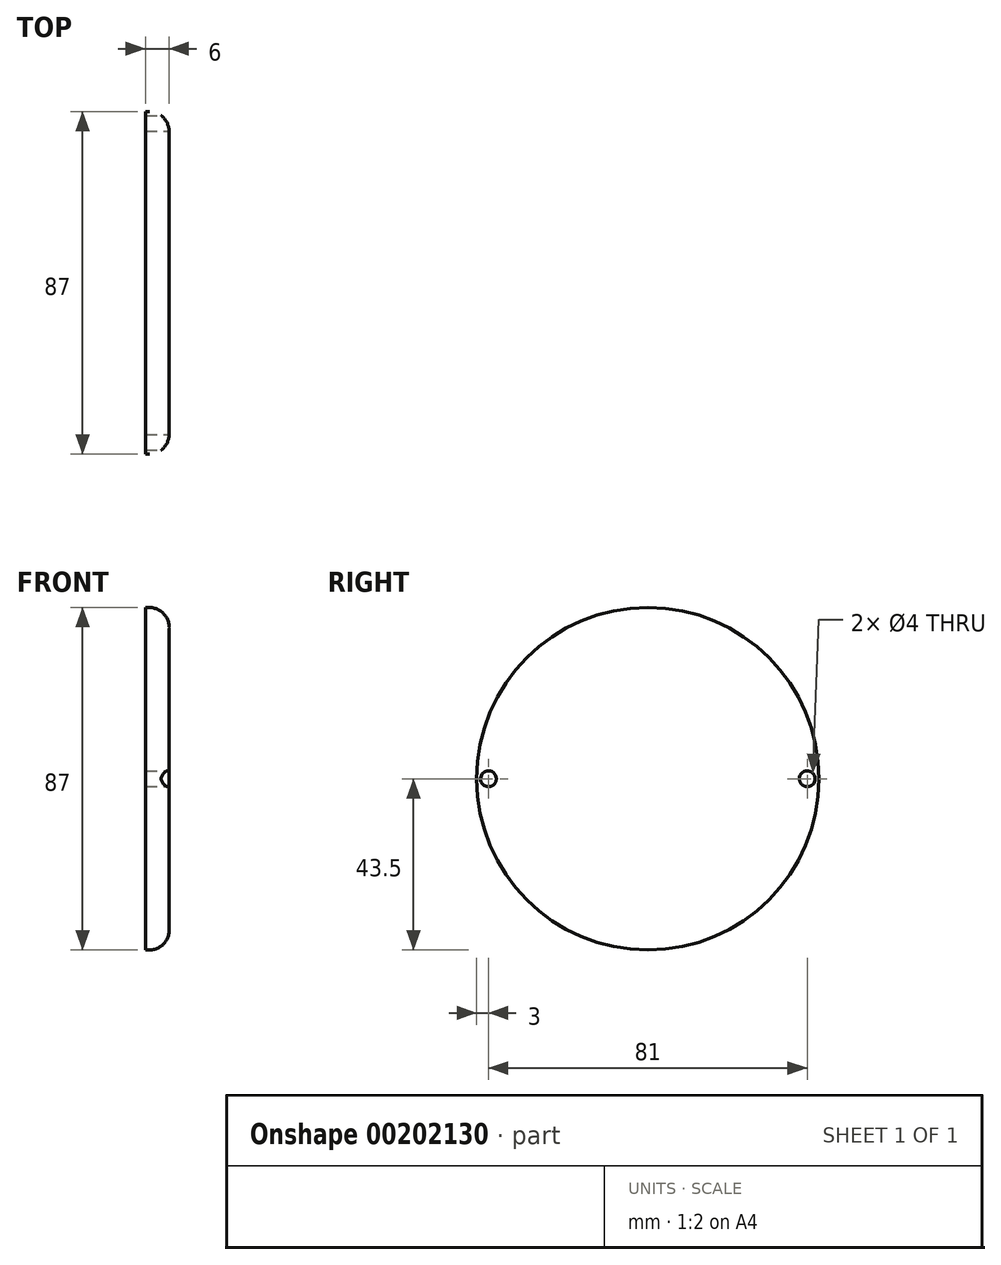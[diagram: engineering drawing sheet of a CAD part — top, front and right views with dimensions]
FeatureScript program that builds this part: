
annotation { "Feature Type Name" : "Feature", "Feature Type Description" : "" }
export const myFeature = defineFeature(function(context is Context, id is Id, definition is map)
    precondition{}
    {
        {
            var Q0;
            Q0=qCreatedBy(makeId("Right.planeOp"),FACE);
            var sketch = newSketch(context, id + "F0", { "sketchPlane" : qUnion([Q0])});
            skCircle(sketch, "E0", {"center": v(0, 0) * mm, "radius": 43.5 * mm});
            skCircle(sketch, "E1", {"center": v(-40.5, 0) * mm, "radius": 2 * mm});
            skCircle(sketch, "E2.MirrorC", {"center": v(40.5, 0) * mm, "radius": 2 * mm});
            skSolve(sketch);
        }
        {
            var Q0;
            Q0=makeQuery(id+"F0.imprint","IMPRINT",FACE,{"disambiguationData":[TD([[makeQuery(id+"F0.imprint","IMPRINT",EDGE,{"derivedFrom":sQuery(id+"F0.wireOp",EDGE,"E0")}),1.0]])]});
            extrude(context, id + "F1", {"entities" : qUnion([Q0]), "oppositeDirection" : true, "depth" : 6 * mm});
        }
        {
            var Q0;
            Q0=makeQuery(id+"F1.opExtrude","CAP_EDGE",EDGE,{"disambiguationData":[OSD([sQuery(id+"F0.wireOp",EDGE,"E0")])],"isStart":true});
            fillet(context, id + "F2", {"entities" : qUnion([Q0]), "radius" : 5 * mm, "tangentPropagation" : true, "allowEdgeOverflow" : false});
        }
    });
